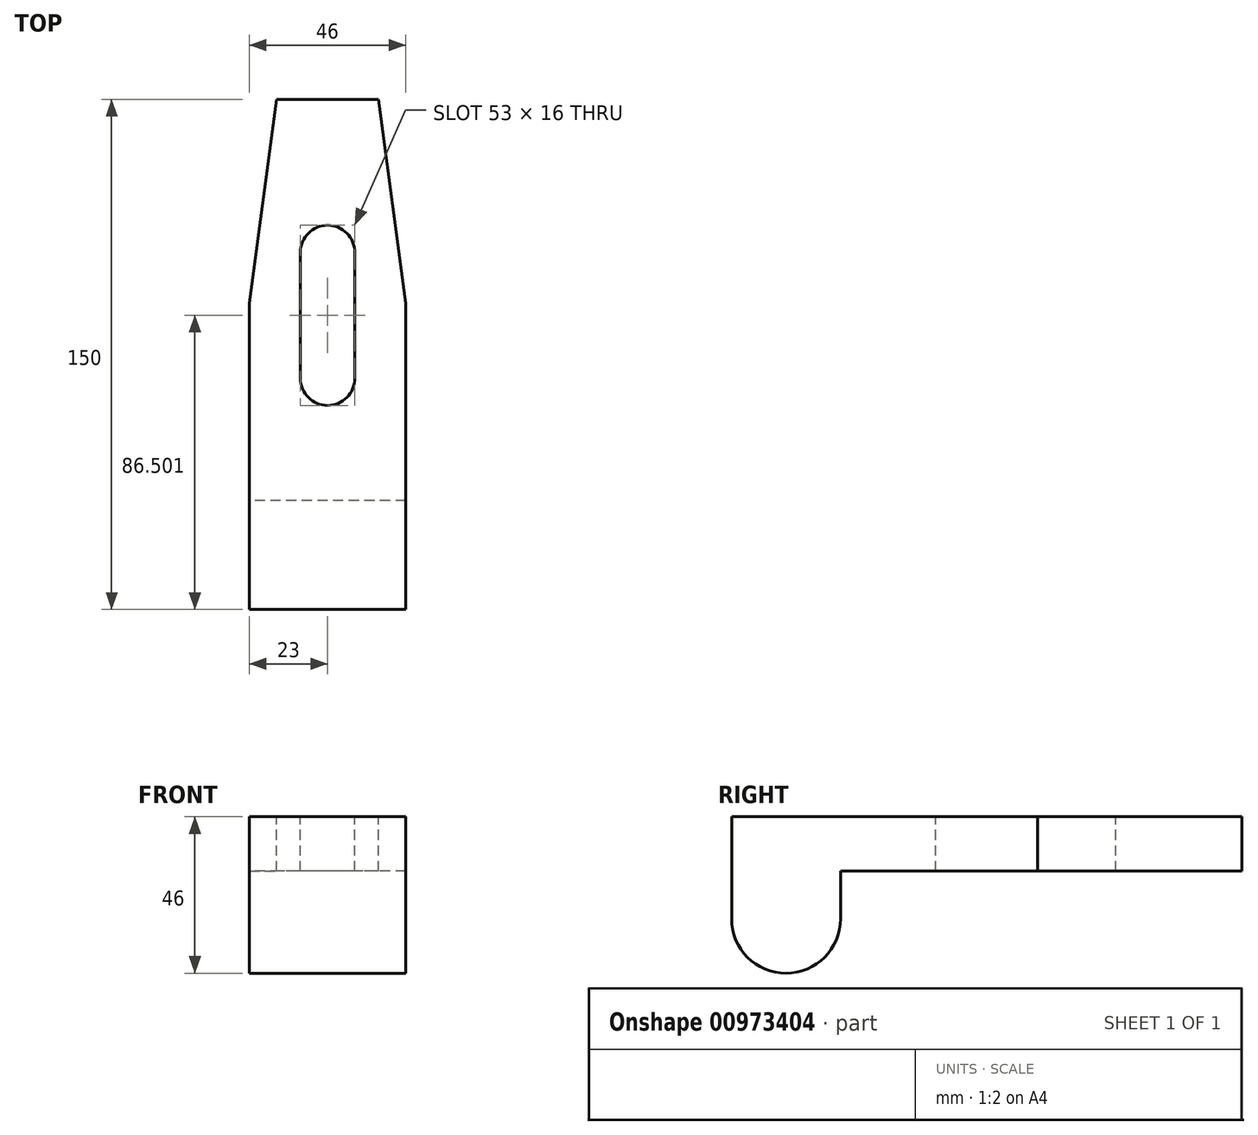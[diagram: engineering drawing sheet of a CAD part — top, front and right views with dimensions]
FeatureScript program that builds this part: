
annotation { "Feature Type Name" : "Feature", "Feature Type Description" : "" }
export const myFeature = defineFeature(function(context is Context, id is Id, definition is map)
    precondition{}
    {
        {
            var Q0;
            Q0=qCreatedBy(makeId("Right.planeOp"),FACE);
            var sketch = newSketch(context, id + "F0", { "sketchPlane" : qUnion([Q0])});
            skLineSegment(sketch, "E0.bottom", {"start": v(76.98, -13.92) * mm, "end": v(-73.02, -13.92) * mm});
            skLineSegment(sketch, "E0.top", {"start": v(76.98, -29.92) * mm, "end": v(-41.02, -29.92) * mm});
            skLineSegment(sketch, "E0.left", {"start": v(76.98, -13.92) * mm, "end": v(76.98, -29.92) * mm});
            skLineSegment(sketch, "E0.right", {"start": v(-73.02, -13.92) * mm, "end": v(-73.02, -29.92) * mm});
            skLineSegment(sketch, "E1.bottom", {"start": v(-73.02, -13.92) * mm, "end": v(-41.02, -13.92) * mm});
            skLineSegment(sketch, "E1.left", {"start": v(-73.02, -13.92) * mm, "end": v(-73.02, -43.92) * mm});
            skLineSegment(sketch, "E1.right", {"start": v(-41.02, -29.92) * mm, "end": v(-41.02, -43.92) * mm});
            skArc(sketch, "E2", {"start": v(-73.02, -43.92) * mm, "mid": v(-57.02, -59.92) * mm, "end": v(-41.02, -43.92) * mm});
            skSolve(sketch);
        }
        {
            var Q0;
            Q0 = qSketchRegion(id + "F0", true);
            extrude(context, id + "F1", {"entities" : qUnion([Q0]), "depth" : 46 * mm, "offsetDistance" : 25 * mm});
        }
        {
            var Q0;
            Q0=makeQuery(id+"F1.opExtrude","SWEPT_FACE",FACE,{"disambiguationData":[OSD([sQuery(id+"F0.wireOp",EDGE,"E0.bottom"),sQuery(id+"F0.wireOp",EDGE,"E1.bottom")])]});
            var sketch = newSketch(context, id + "F2", { "sketchPlane" : qUnion([Q0])});
            skLineSegment(sketch, "E3.bottom", {"start": v(38, 76.98) * mm, "end": v(8, 76.98) * mm});
            skLineSegment(sketch, "E3.top", {"start": v(46, 16.98) * mm, "end": v(0, 16.98) * mm});
            skLineSegment(sketch, "E4", {"start": v(46, 16.98) * mm, "end": v(40.15, 16.98) * mm});
            skLineSegment(sketch, "E5", {"start": v(40.15, 16.98) * mm, "end": v(0, 16.98) * mm});
            skLineSegment(sketch, "E6", {"start": v(38, 76.98) * mm, "end": v(46, 16.98) * mm});
            skLineSegment(sketch, "E7", {"start": v(8, 77.02) * mm, "end": v(0, 16.98) * mm});
            skPoint(sketch, "E8.end.orphan", {"position": v(0, 76.98) * mm});
            skPoint(sketch, "E9.orphan", {"position": v(46, 76.98) * mm});
            skSolve(sketch);
        }
        {
            var Q0;
            {var subQ0=sQuery(id+"F2.wireOp",EDGE,"E6");Q0=makeQuery(id+"F2.imprint","IMPRINT",FACE,{"disambiguationData":[TD([[makeQuery(id+"F2.imprint","IMPRINT",EDGE,{"derivedFrom":subQ0}),1.0]])]});}
            var Q1;
            {var subQ0=sQuery(id+"F2.wireOp",EDGE,"E7");var subQ1=sQuery(id+"F0.wireOp",EDGE,"E0.bottom");var subQ2=makeQuery(id+"F1.opExtrude","CAP_EDGE",EDGE,{"disambiguationData":[OSD([subQ1,sQuery(id+"F0.wireOp",EDGE,"E1.bottom")])],"isStart":true});var subQ3=makeQuery(id+"F2.imprint","INTERSECT",VERTEX,{"derivedFrom":[subQ2,sQuery(id+"F2.wireOp",EDGE,"E5"),subQ0]});Q1=makeQuery(id+"F2.imprint","IMPRINT",FACE,{"disambiguationData":[TD([[makeQuery(id+"F2.imprint","IMPRINT",EDGE,{"disambiguationData":[TD([[subQ3,1.0]])],"derivedFrom":subQ0}),-1.0]])]});}
            extrude(context, id + "F3", {"entities" : qUnion([Q0, Q1]), "operationType" : NewBodyOperationType.REMOVE, "oppositeDirection" : true, "depth" : 25 * mm, "offsetDistance" : 25 * mm});
        }
        {
            var Q0;
            Q0=makeQuery(id+"F1.opExtrude","SWEPT_FACE",FACE,{"disambiguationData":[OSD([sQuery(id+"F0.wireOp",EDGE,"E0.bottom"),sQuery(id+"F0.wireOp",EDGE,"E1.bottom")])]});
            var sketch = newSketch(context, id + "F4", { "sketchPlane" : qUnion([Q0])});
            skLineSegment(sketch, "E10", {"start": v(15, 31.98) * mm, "end": v(15, -5.02) * mm});
            skLineSegment(sketch, "E11", {"start": v(31, 31.98) * mm, "end": v(31, -5.02) * mm});
            skArc(sketch, "E12", {"start": v(31, 31.98) * mm, "mid": v(23, 39.98) * mm, "end": v(15, 31.98) * mm});
            skArc(sketch, "E13", {"start": v(15, -5.02) * mm, "mid": v(23, -13.02) * mm, "end": v(31, -5.02) * mm});
            skSolve(sketch);
        }
        {
            var Q0;
            Q0 = qSketchRegion(id + "F4", true);
            extrude(context, id + "F5", {"entities" : qUnion([Q0]), "operationType" : NewBodyOperationType.REMOVE, "oppositeDirection" : true, "depth" : 25 * mm, "offsetDistance" : 25 * mm});
        }
    });
